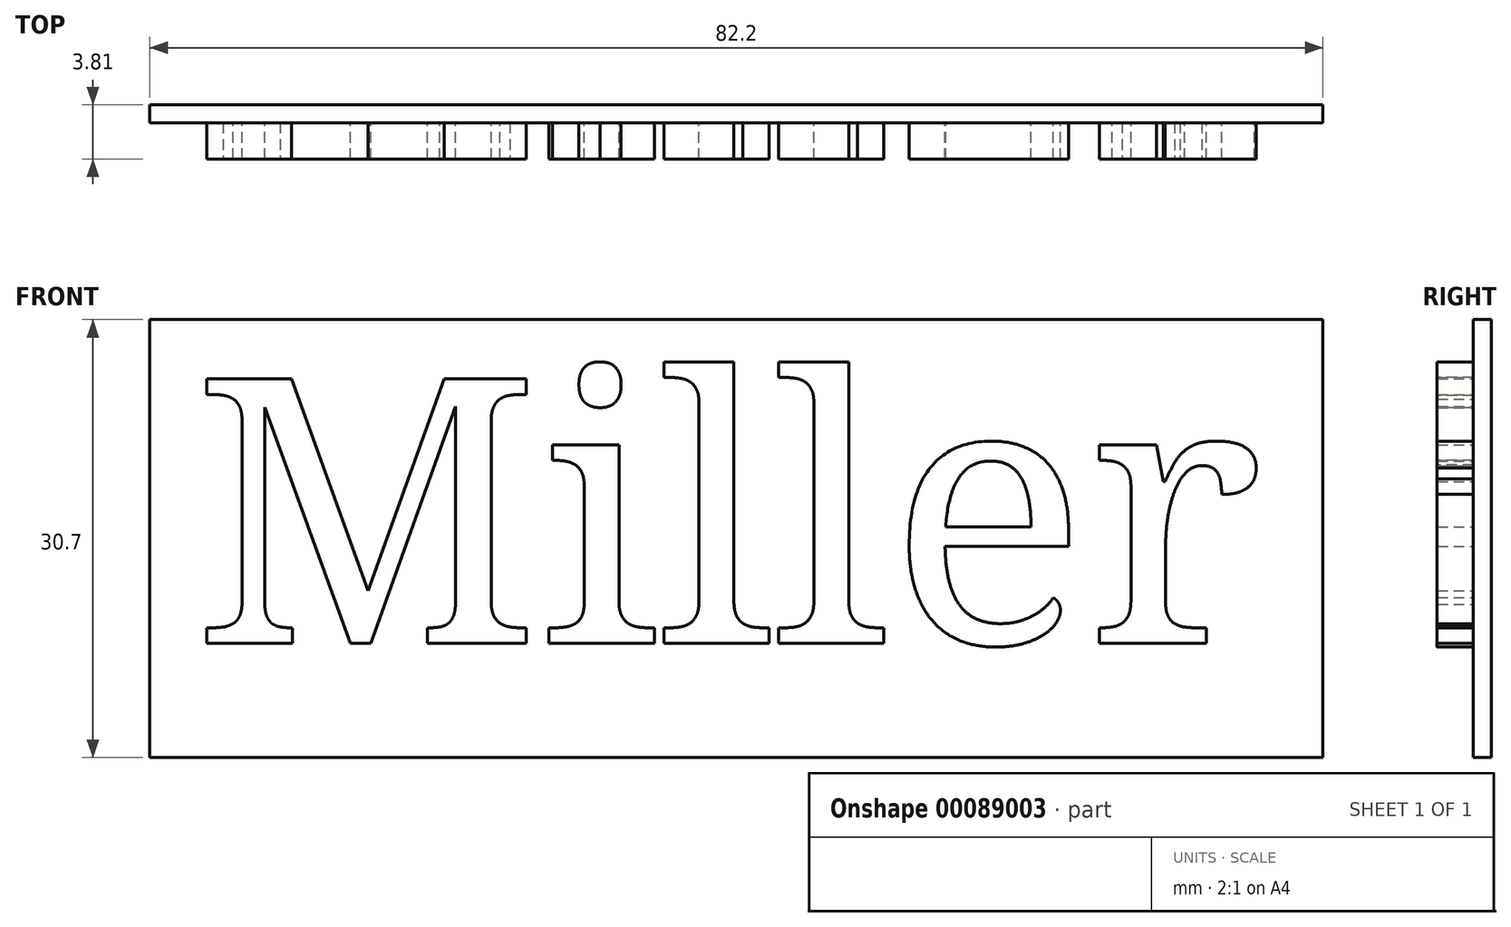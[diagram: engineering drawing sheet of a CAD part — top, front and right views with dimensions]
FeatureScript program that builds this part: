
annotation { "Feature Type Name" : "Feature", "Feature Type Description" : "" }
export const myFeature = defineFeature(function(context is Context, id is Id, definition is map)
    precondition{}
    {
        {
            var Q0;
            Q0=qCreatedBy(makeId("Front.planeOp"),FACE);
            var sketch = newSketch(context, id + "F0", { "sketchPlane" : qUnion([Q0])});
            skText(sketch, "E0", { "text": "Miller", "fontName": "NotoSerif-Regular.ttf"});
            skPoint(sketch, "E1.middle", {"position": v(0, 0) * mm});
            const initialGuessF0  = {"E0": [-0.0381, -0.01067, 1, 0, 0.0187]};
            skSetInitialGuess(sketch, initialGuessF0);
            skSolve(sketch);
        }
        {
            var Q0;
            Q0=qCreatedBy(makeId("Front.planeOp"),FACE);
            var sketch = newSketch(context, id + "F1", { "sketchPlane" : qUnion([Q0])});
            skLineSegment(sketch, "E2.bottom", {"start": v(-41.1, 12.03) * mm, "end": v(41.1, 12.03) * mm});
            skLineSegment(sketch, "E2.top", {"start": v(-41.1, -18.67) * mm, "end": v(41.1, -18.67) * mm});
            skLineSegment(sketch, "E2.left", {"start": v(-41.1, 12.03) * mm, "end": v(-41.1, -18.67) * mm});
            skLineSegment(sketch, "E2.right", {"start": v(41.1, 12.03) * mm, "end": v(41.1, -18.67) * mm});
            skSolve(sketch);
        }
        {
            var Q0;
            Q0 = qSketchRegion(id + "F0", true);
            extrude(context, id + "F2", {"entities" : qUnion([Q0]), "depth" : 2.54 * mm});
        }
        {
            var Q0;
            Q0=makeQuery(id+"F1.imprint","IMPRINT",FACE,{"disambiguationData":[TD([[makeQuery(id+"F1.imprint","IMPRINT",EDGE,{"derivedFrom":sQuery(id+"F1.wireOp",EDGE,"E2.bottom")}),-1.0]])]});
            extrude(context, id + "F3", {"entities" : qUnion([Q0]), "operationType" : NewBodyOperationType.ADD, "oppositeDirection" : true, "depth" : 1.27 * mm});
        }
    });
